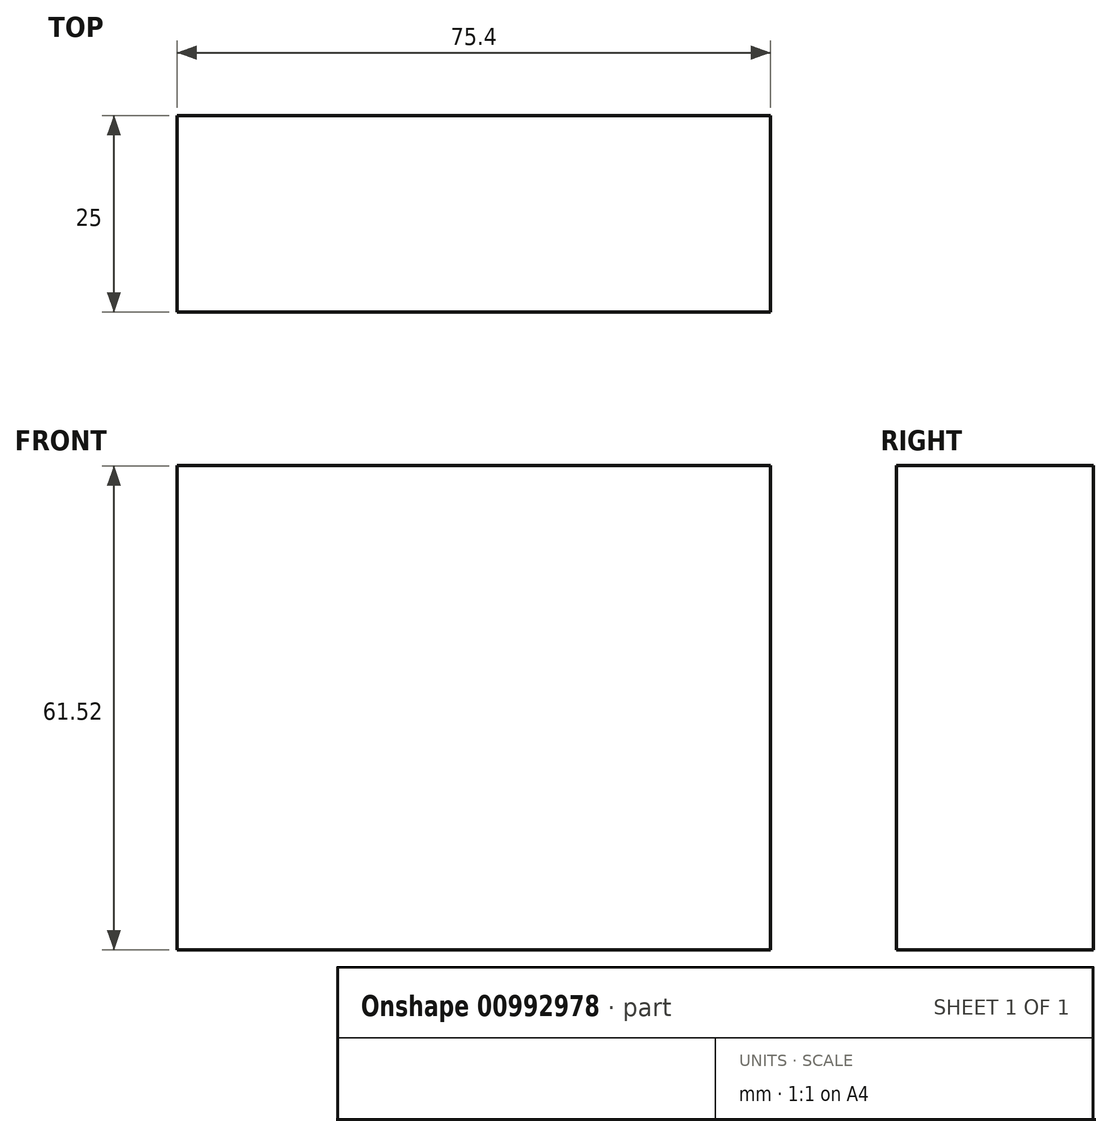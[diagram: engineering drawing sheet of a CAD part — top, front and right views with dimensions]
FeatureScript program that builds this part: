
annotation { "Feature Type Name" : "Feature", "Feature Type Description" : "" }
export const myFeature = defineFeature(function(context is Context, id is Id, definition is map)
    precondition{}
    {
        {
            var Q0;
            Q0=qCreatedBy(makeId("Front.planeOp"),FACE);
            var sketch = newSketch(context, id + "F0", { "sketchPlane" : qUnion([Q0])});
            skLineSegment(sketch, "E0.bottom", {"start": v(-135.16, 26.88) * mm, "end": v(-59.76, 26.88) * mm});
            skLineSegment(sketch, "E0.top", {"start": v(-135.16, -34.64) * mm, "end": v(-59.76, -34.64) * mm});
            skLineSegment(sketch, "E0.left", {"start": v(-135.16, 26.88) * mm, "end": v(-135.16, -34.64) * mm});
            skLineSegment(sketch, "E0.right", {"start": v(-59.76, 26.88) * mm, "end": v(-59.76, -34.64) * mm});
            skSolve(sketch);
        }
        {
            var Q0;
            Q0 = qSketchRegion(id + "F0", true);
            extrude(context, id + "F1", {"entities" : qUnion([Q0]), "depth" : 25 * mm, "offsetDistance" : 25 * mm});
        }
    });
